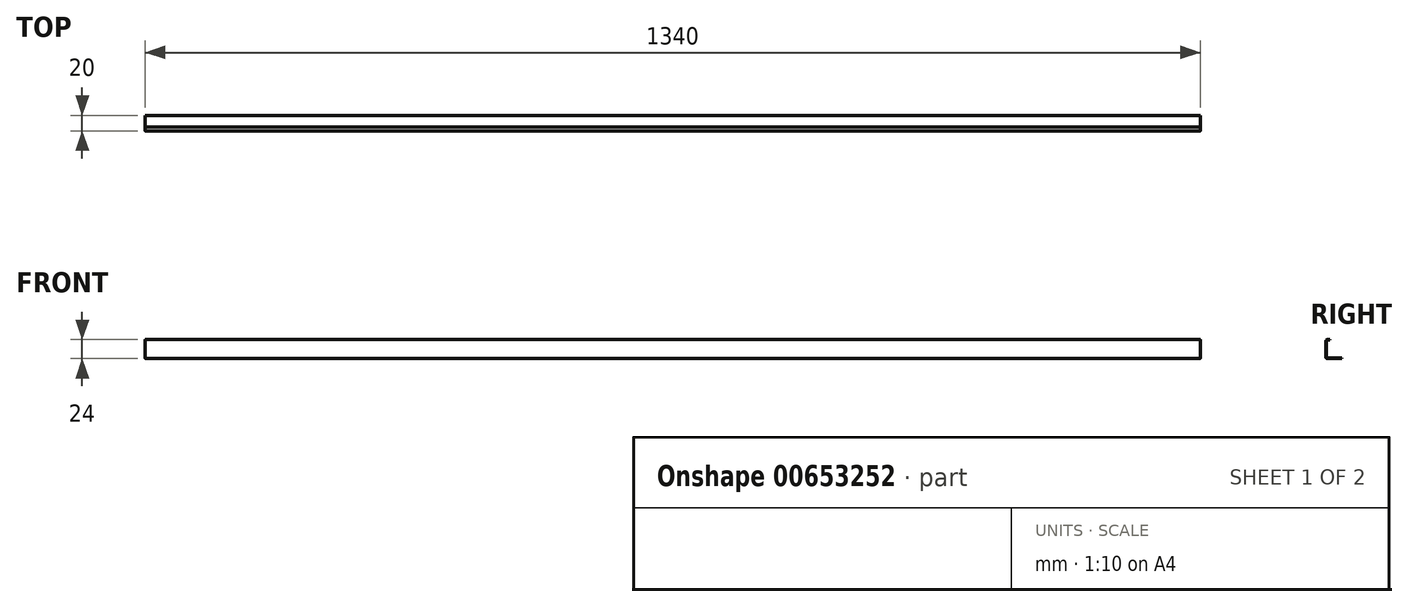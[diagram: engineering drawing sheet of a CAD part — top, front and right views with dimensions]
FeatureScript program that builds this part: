
annotation { "Feature Type Name" : "Feature", "Feature Type Description" : "" }
export const myFeature = defineFeature(function(context is Context, id is Id, definition is map)
    precondition{}
    {
        {
            var Q0;
            Q0=qCreatedBy(makeId("Right.planeOp"),FACE);
            var sketch = newSketch(context, id + "F0", { "sketchPlane" : qUnion([Q0])});
            skLineSegment(sketch, "E0", {"start": v(10, -12) * mm, "end": v(-9, -12) * mm});
            skArc(sketch, "E1", {"start": v(-9, -12) * mm, "mid": v(-9.7, -11.7) * mm, "end": v(-10, -11) * mm});
            skLineSegment(sketch, "E2", {"start": v(-10, -11) * mm, "end": v(-10, 11) * mm});
            skArc(sketch, "E3", {"start": v(-10, 11) * mm, "mid": v(-9.7, 11.7) * mm, "end": v(-9, 12) * mm});
            skLineSegment(sketch, "E4", {"start": v(-9, 12) * mm, "end": v(-5, 12) * mm});
            skLineSegment(sketch, "E5", {"start": v(-5, 12) * mm, "end": v(-5, 11.5) * mm});
            skLineSegment(sketch, "E6", {"start": v(-5, 11.5) * mm, "end": v(-9, 11.5) * mm});
            skArc(sketch, "E7", {"start": v(-9, 11.5) * mm, "mid": v(-9.35, 11.35) * mm, "end": v(-9.5, 11) * mm});
            skLineSegment(sketch, "E8", {"start": v(-9.5, 11) * mm, "end": v(-9.5, -11) * mm});
            skArc(sketch, "E9", {"start": v(-9.5, -11) * mm, "mid": v(-9.35, -11.35) * mm, "end": v(-9, -11.5) * mm});
            skLineSegment(sketch, "E10", {"start": v(-9, -11.5) * mm, "end": v(10, -11.5) * mm});
            skLineSegment(sketch, "E11", {"start": v(10, -11.5) * mm, "end": v(10, -12) * mm});
            skSolve(sketch);
        }
        {
            var Q0;
            Q0=qSketchRegion(id+"F0",true);
            extrude(context, id + "F1", {"entities" : qUnion([Q0]), "oppositeDirection" : true, "depth" : 1340 * mm, "offsetDistance" : 25 * mm});
        }
    });
